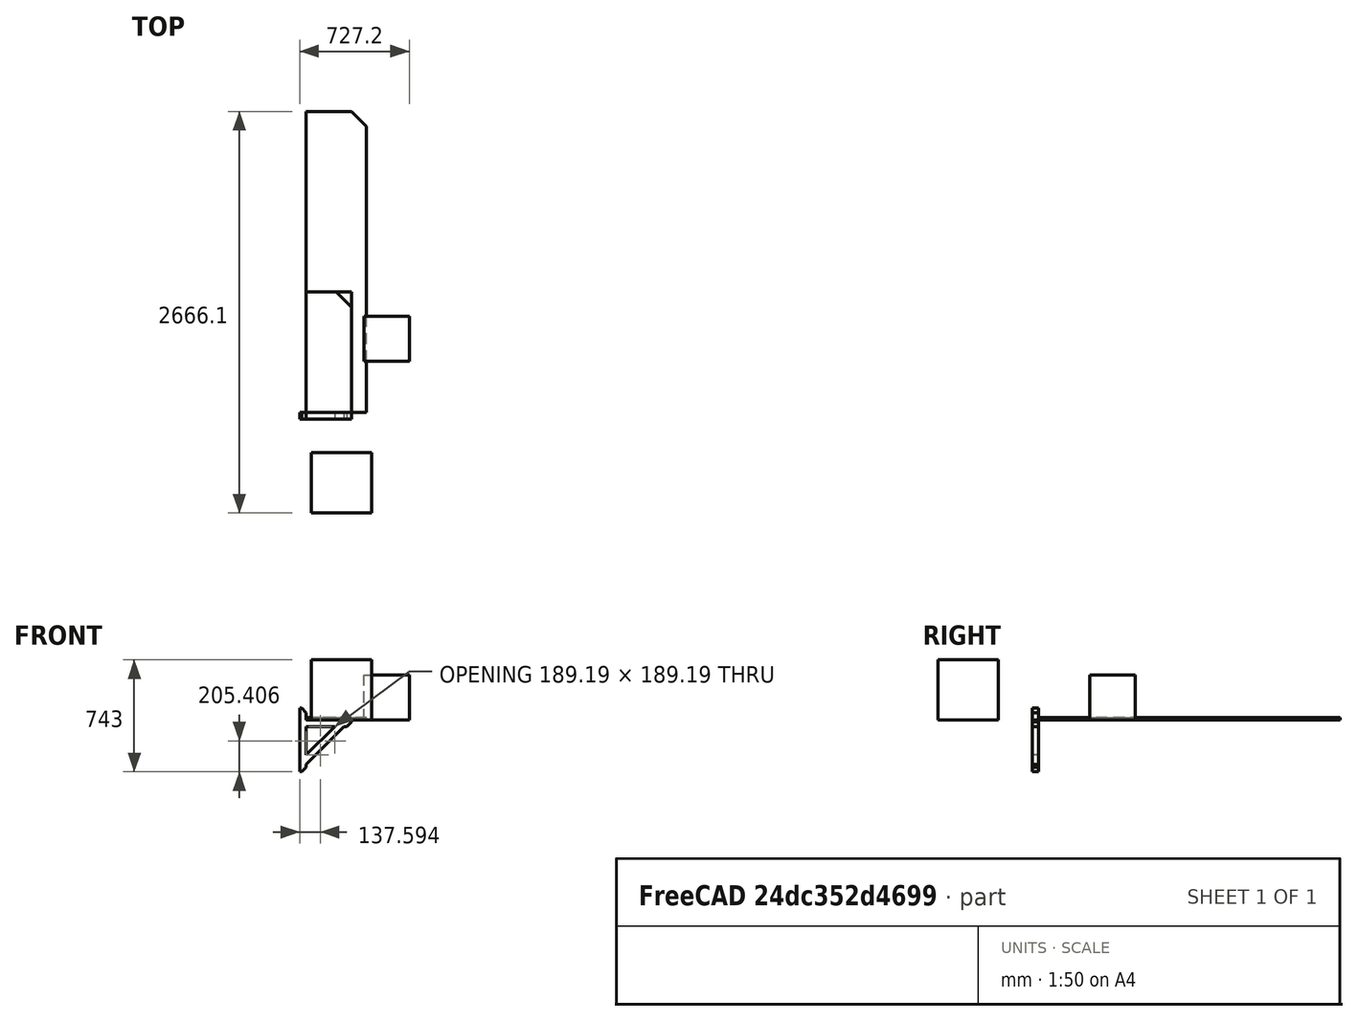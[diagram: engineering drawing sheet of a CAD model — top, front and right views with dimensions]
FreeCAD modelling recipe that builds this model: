
FCSTD DOCUMENT  (FreeCAD 1.0R39109 (Git))
Label: shed_shelves
License: All rights reserved
LicenseURL: https://en.wikipedia.org/wiki/All_rights_reserved
objects: App::FeaturePython×9, App::Link×7, App::Part×5, Sketcher::SketchObject×4, PartDesign::Pad×4, PartDesign::Body×4, Part::Box×2, PartDesign::Chamfer×2, App::DocumentObjectGroup×1, Assembly::JointGroup×1, Assembly::AssemblyObject×1
note: 32 computed .brp shape members not serialized (recipe doc carries the construction recipe); baked Part::Feature solids carry a one-line shape summary decoded from their .brp

FEATURE [Sketcher::SketchObject] Sketch
  ArcFitTolerance = 1e-06
  AttachmentSupport = -> [XY_Plane]
  FullyConstrained = true
  MakeInternals = false
  MapMode = 5
  sketch-geometry (4):
    g0: LineSegment StartX=0 StartY=0 StartZ=0 EndX=400 EndY=0 EndZ=0
    g1: LineSegment StartX=400 StartY=0 StartZ=0 EndX=400 EndY=2000 EndZ=0
    g2: LineSegment StartX=400 StartY=2000 StartZ=0 EndX=0 EndY=2000 EndZ=0
    g3: LineSegment StartX=0 StartY=2000 StartZ=0 EndX=0 EndY=0 EndZ=0
  constraints (11):
    c: Coincident(g0,g1)
    c: Coincident(g1,g2)
    c: Coincident(g2,g3)
    c: Coincident(g3,g0)
    c: Horizontal(g0)
    c: Horizontal(g2)
    c: Vertical(g1)
    c: Vertical(g3)
    c: Distance(g1,g3) = 400
    c: Distance(g0,g2) = 2000
    c: Coincident(g0,g-1)
FEATURE [PartDesign::Pad] Pad
  Direction = (0,0,1)
  Length = 18
  Length2 = 10
  Profile = -> Sketch
  ReferenceAxis = -> Sketch [N_Axis]
  Refine = true
  Suppressed = false
  Type = 0
FEATURE [Sketcher::SketchObject] Sketch001
  ArcFitTolerance = 1e-06
  AttachmentSupport = -> [XY_Plane002]
  FullyConstrained = true
  MakeInternals = false
  MapMode = 5
  sketch-geometry (4):
    g0: LineSegment StartX=0 StartY=0 StartZ=0 EndX=300 EndY=0 EndZ=0
    g1: LineSegment StartX=300 StartY=0 StartZ=0 EndX=300 EndY=800 EndZ=0
    g2: LineSegment StartX=300 StartY=800 StartZ=0 EndX=0 EndY=800 EndZ=0
    g3: LineSegment StartX=0 StartY=800 StartZ=0 EndX=0 EndY=0 EndZ=0
  constraints (11):
    c: Coincident(g0,g1)
    c: Coincident(g1,g2)
    c: Coincident(g2,g3)
    c: Coincident(g3,g0)
    c: Horizontal(g0)
    c: Horizontal(g2)
    c: Vertical(g1)
    c: Vertical(g3)
    c: Distance(g1,g3) = 300
    c: Distance(g0,g2) = 800
    c: Coincident(g0,g-1)
FEATURE [PartDesign::Pad] Pad001
  Direction = (0,0,1)
  Length = 18
  Length2 = 10
  Profile = -> Sketch001
  ReferenceAxis = -> Sketch001 [N_Axis]
  Refine = true
  Suppressed = false
  Type = 0
FEATURE [PartDesign::Body] Body001
  AllowCompound = false
  Group = -> [Sketch001,Pad001]
  Origin = -> Origin002
  Tip = -> Pad001
FEATURE [App::Part] Part001  label="Part_800x400x18"
  Group = -> [Body001]
  Origin = -> Origin003
FEATURE [Sketcher::SketchObject] Sketch002
  ArcFitTolerance = 1e-06
  AttachmentSupport = -> [XY_Plane004]
  FullyConstrained = true
  MakeInternals = false
  MapMode = 5
  sketch-geometry (4):
    g0: LineSegment StartX=0 StartY=0 StartZ=0 EndX=300 EndY=0 EndZ=0
    g1: LineSegment StartX=300 StartY=0 StartZ=0 EndX=300 EndY=800 EndZ=0
    g2: LineSegment StartX=300 StartY=800 StartZ=0 EndX=0 EndY=800 EndZ=0
    g3: LineSegment StartX=0 StartY=800 StartZ=0 EndX=0 EndY=0 EndZ=0
  constraints (11):
    c: Coincident(g0,g1)
    c: Coincident(g1,g2)
    c: Coincident(g2,g3)
    c: Coincident(g3,g0)
    c: Horizontal(g0)
    c: Horizontal(g2)
    c: Vertical(g1)
    c: Vertical(g3)
    c: Distance(g1,g3) = 300
    c: Distance(g0,g2) = 800
    c: Coincident(g0,g-1)
FEATURE [PartDesign::Pad] Pad002
  Direction = (0,0,1)
  Length = 18
  Length2 = 10
  Profile = -> Sketch002
  ReferenceAxis = -> Sketch002 [N_Axis]
  Refine = true
  Suppressed = false
  Type = 0
FEATURE [App::Link] Part_800x30x18  label="Part_800x30x019"
  LinkPlacement = pos=(0,0,0) rot=(0,0,1;4.71239rad)
  LinkedObject = -> Part002
  Placement = pos=(0,0,0) rot=(0,0,1;4.71239rad)
FEATURE [App::FeaturePython] GroundedJoint  # Assembly grounded joint (typed FeaturePython)
  ObjectToGround = -> Part_800x30x18
  Placement = pos=(0,0,0) rot=(0,0,1;4.71239rad)
FEATURE [App::Link] Part_800x400x18  label="Part_800x400x019"
  LinkPlacement = pos=(-300,-800,0) rot=(0,0,1;0rad)
  LinkedObject = -> Part001
  Placement = pos=(-300,-800,0) rot=(0,0,1;0rad)
FEATURE [App::Link] Part_2000x400x18  label="Part_2000x400x019"
  LinkPlacement = pos=(-300,-2800,0) rot=(0,0,1;0rad)
  LinkedObject = -> Part
  Placement = pos=(-300,-2800,0) rot=(0,0,1;0rad)
FEATURE [Part::Box] Box  label="Cube"
  AttacherType = Attacher::AttachEngine3D
  Height = 300
  Length = 300
  Placement = pos=(384.2,340,0) rot=(0,0,1;0rad)
  Width = 300
FEATURE [Part::Box] Box001  label="Cube001"
  AttacherType = Attacher::AttachEngine3D
  Height = 400
  Length = 400
  Placement = pos=(35,-666.1,0) rot=(0,0,1;0rad)
  Width = 400
FEATURE [App::Part] Part003
  Group = -> [Box,Box001]
  Origin = -> Origin007
  Placement = pos=(-336.4,-642.4,18) rot=(0,0,1;0rad)
FEATURE [PartDesign::Chamfer] Chamfer
  Angle = 45
  Base = -> Pad [Edge5]
  BaseFeature = -> Pad
  ChamferType = 0
  FlipDirection = false
  Refine = true
  Size = 100
  Size2 = 1
  SupportTransform = false
  Suppressed = false
  UseAllEdges = false
FEATURE [PartDesign::Body] Body
  AllowCompound = false
  Group = -> [Sketch,Pad,Chamfer]
  Origin = -> Origin
  Tip = -> Chamfer
FEATURE [App::Part] Part  label="Part_2000x400x18"
  Group = -> [Body]
  Origin = -> Origin001
FEATURE [PartDesign::Chamfer] Chamfer001
  Angle = 45
  Base = -> Pad002 [Edge5]
  BaseFeature = -> Pad002
  ChamferType = 0
  FlipDirection = false
  Refine = true
  Size = 100
  Size2 = 1
  SupportTransform = false
  Suppressed = false
  UseAllEdges = false
FEATURE [PartDesign::Body] Body002
  AllowCompound = false
  Group = -> [Sketch002,Pad002,Chamfer001]
  Origin = -> Origin004
  Tip = -> Chamfer001
FEATURE [App::Part] Part002  label="Part_800x30x18"
  Group = -> [Body002]
  Origin = -> Origin005
FEATURE [App::DocumentObjectGroup] Group  label="ShelvePlates"
  Group = -> [Part002,Part001,Part]
FEATURE [Sketcher::SketchObject] Sketch003
  ArcFitTolerance = 1e-06
  AttachmentSupport = -> [XZ_Plane009]
  FullyConstrained = true
  MakeInternals = false
  MapMode = 5
  Placement = pos=(0,0,0) rot=(1,0,0;1.5708rad)
  expr: Constraints[52] = .Constraints.edgeradii
  expr: Constraints[53] = .Constraints.edgeradii
  expr: Constraints[54] = .Constraints.wood_thinckness
  expr: Constraints[66] = .Constraints.wood_thinckness
  sketch-geometry (32):
    g0: LineSegment StartX=-43 StartY=80 StartZ=0 EndX=-43 EndY=-343 EndZ=0
    g1: LineSegment StartX=-43 StartY=-343 StartZ=0 EndX=-30 EndY=-343 EndZ=0
    g2: LineSegment StartX=0 StartY=-313 StartZ=0 EndX=0 EndY=50 EndZ=0
    g3: LineSegment StartX=-30 StartY=80 StartZ=0 EndX=-43 EndY=80 EndZ=0
    g4: LineSegment StartX=0 StartY=0 StartZ=0 EndX=0 EndY=-43 EndZ=0
    g5: LineSegment StartX=0 StartY=-43 StartZ=0 EndX=270 EndY=-43 EndZ=0
    g6: LineSegment StartX=300 StartY=-13 StartZ=0 EndX=300 EndY=0 EndZ=0
    g7: LineSegment StartX=300 StartY=0 StartZ=0 EndX=0 EndY=0 EndZ=0
    g8: LineSegment [constr] StartX=0 StartY=0 StartZ=0 EndX=400 EndY=0 EndZ=0
    g9: LineSegment [constr] StartX=400 StartY=0 StartZ=0 EndX=400 EndY=18 EndZ=0
    g10: LineSegment [constr] StartX=400 StartY=18 StartZ=0 EndX=0 EndY=18 EndZ=0
    g11: LineSegment [constr] StartX=0 StartY=18 StartZ=0 EndX=0 EndY=0 EndZ=0
    g12: LineSegment [constr] StartX=-43 StartY=-343 StartZ=0 EndX=300 EndY=0 EndZ=0
    g13: ArcOfCircle [constr] CenterX=-30 CenterY=50 CenterZ=0 NormalX=0 NormalY=0 NormalZ=1 AngleXU=0 Radius=30 StartAngle=0 EndAngle=1.5708
    g14: GeomPoint [constr] X=0 Y=80 Z=0
    g15: LineSegment StartX=0 StartY=50 StartZ=0 EndX=-30 EndY=80 EndZ=0
    g16: ArcOfCircle [constr] CenterX=270 CenterY=-13 CenterZ=0 NormalX=0 NormalY=0 NormalZ=1 AngleXU=0 Radius=30 StartAngle=4.71239 EndAngle=6.28319
    g17: GeomPoint [constr] X=300 Y=-43 Z=0
    g18: LineSegment StartX=270 StartY=-43 StartZ=0 EndX=300 EndY=-13 EndZ=0
    g19: ArcOfCircle [constr] CenterX=-30 CenterY=-313 CenterZ=0 NormalX=0 NormalY=0 NormalZ=1 AngleXU=0 Radius=30 StartAngle=4.71239 EndAngle=6.28319
    g20: GeomPoint [constr] X=0 Y=-343 Z=0
    g21: LineSegment StartX=-30 StartY=-343 StartZ=0 EndX=0 EndY=-313 EndZ=0
    g22: LineSegment StartX=3.6e-15 StartY=-293 StartZ=0 EndX=250 EndY=-43 EndZ=0
    g23: LineSegment [constr] StartX=-30.4056 StartY=-262.594 StartZ=0 EndX=219.594 EndY=-12.5944 EndZ=0
    g24: LineSegment [constr] StartX=-30.4056 StartY=-262.594 StartZ=0 EndX=3.6e-15 EndY=-293 EndZ=0
    g25: LineSegment [constr] StartX=219.594 StartY=-12.5944 StartZ=0 EndX=250 EndY=-43 EndZ=0
    g26: LineSegment StartX=3.6e-15 StartY=-293 StartZ=0 EndX=3.6e-15 EndY=-232.189 EndZ=0
    g27: LineSegment StartX=3.6e-15 StartY=-232.189 StartZ=0 EndX=189.189 EndY=-43 EndZ=0
    g28: LineSegment StartX=189.189 StartY=-43 StartZ=0 EndX=250 EndY=-43 EndZ=0
    g29: LineSegment [constr] StartX=-30 StartY=-343 StartZ=0 EndX=-43 EndY=-356 EndZ=0
    g30: LineSegment [constr] StartX=-30 StartY=80 StartZ=0 EndX=-43 EndY=93 EndZ=0
    g31: LineSegment [constr] StartX=-43 StartY=93 StartZ=0 EndX=-43 EndY=-356 EndZ=0
  constraints (88):
    c: Coincident(g3,g0)
    c: Vertical(g0)
    c: Vertical(g2)
    c: Horizontal(g1)
    c: Horizontal(g3)
    c: Coincident(g4,g5)
    c: Coincident(g6,g7)
    c: Coincident(g7,g4)
    c: Vertical(g4)
    c: Vertical(g6)
    c: Horizontal(g5)
    c: Horizontal(g7)
    c: PointOnObject(g4,g2)
    c: Distance(g17,g6) = 43  'wood_thinckness'
    c: Distance(g14,g4) = 80
    c: Coincident(g8,g9)
    c: Coincident(g9,g10)
    c: Coincident(g10,g11)
    c: Coincident(g11,g8)
    c: Horizontal(g8)
    c: Horizontal(g10)
    c: Vertical(g9)
    c: Vertical(g11)
    c: Coincident(g8,g-1)
    c: DistanceX(g10,g10) = 400
    c: Distance(g9,g9) = 18
    c: Coincident(g1,g0)
    c: Coincident(g4,g8)
    c: Coincident(g12,g0)
    c: Coincident(g12,g6)
    c: Angle(g10,g12) = 0.785398
    c: DistanceY(g0,g0) = 423
    c: Distance(g8,g6) = 100
    c: PointOnObject(g14,g2)
    c: PointOnObject(g14,g3)
    c: Tangent(g2,g13) = -1.5708
    c: Tangent(g3,g13) = -1.5708
    c: Coincident(g15,g2)
    c: Coincident(g15,g3)
    c: PointOnObject(g17,g5)
    c: PointOnObject(g17,g6)
    c: Tangent(g5,g16) = -1.5708
    c: Tangent(g6,g16) = -1.5708
    c: Coincident(g18,g5)
    c: Coincident(g18,g6)
    c: PointOnObject(g20,g1)
    c: PointOnObject(g20,g2)
    c: Tangent(g1,g19) = -1.5708
    c: Tangent(g2,g19) = -1.5708
    c: Coincident(g21,g1)
    c: Coincident(g21,g2)
    c: Radius(g16) = 30  'edgeradii'
    c: Radius(g19) = 30
    c: Radius(g13) = 30
    c: Distance(g0,g2) = 43
    c: DistanceX(g7,g7) = 300
    c: PointOnObject(g22,g2)
    c: PointOnObject(g22,g5)
    c: Parallel(g23,g22)
    c: Coincident(g24,g23)
    c: Coincident(g24,g22)
    c: Coincident(g25,g22)
    c: Coincident(g23,g25)
    c: Parallel(g24,g25)
    c: Perpendicular(g25,g23,g23) = 1.5708
    c: Parallel(g22,g12)
    c: Distance(g25,g25) = 43
    c: Coincident(g22,g26)
    c: PointOnObject(g26,g23)
    c: Vertical(g26)
    c: Coincident(g26,g27)
    c: Coincident(g28,g22)
    c: Coincident(g28,g27)
    c: PointOnObject(g27,g23)
    c: PointOnObject(g27,g5)
    c: Distance(g22,g22) = 353.553
    c: Distance(g2,g4) = 50
    c: Distance(g2,g22) = 20
    c: Coincident(g29,g1)
    c: Coincident(g30,g3)
    c: Parallel(g15,g30)
    c: Parallel(g29,g21)
    c: Coincident(g31,g30)
    c: Coincident(g31,g29)
    c: Vertical(g31)
    c: Vertical(g29,g0)
    c: DistanceY(g29,g30) = 449
    c: DistanceY(g29,g22) = 63
FEATURE [PartDesign::Pad] Pad003
  Direction = (0,-1,2e-16)
  Length = 43
  Length2 = 10
  Placement = pos=(0,0,0) rot=(1,0,0;1.5708rad)
  Profile = -> Sketch003
  ReferenceAxis = -> Sketch003 [N_Axis]
  Refine = true
  Suppressed = false
  Type = 0
FEATURE [PartDesign::Body] Body003
  AllowCompound = false
  Group = -> [Sketch003,Pad003]
  Origin = -> Origin009
  Tip = -> Pad003
FEATURE [App::Part] Part004  label="shelf_boy"
  Group = -> [Body003]
  Origin = -> Origin008
FEATURE [App::Link] shelf_boy  label="shelf_boy001"
  LinkPlacement = pos=(-300,-2688.5,-4.8e-15) rot=(0,0,1;0rad)
  LinkedObject = -> Part004
  Placement = pos=(-300,-2688.5,-4.8e-15) rot=(0,0,1;0rad)
FEATURE [App::Link] shelf_boy001  label="shelf_boy002"
  LinkPlacement = pos=(-300,-778.5,-4.8e-15) rot=(0,0,1;0rad)
  LinkedObject = -> Part004
  Placement = pos=(-300,-778.5,-4.8e-15) rot=(0,0,1;0rad)
FEATURE [App::Link] shelf_boy002  label="shelf_boy003"
  LinkPlacement = pos=(21.5,-1.11e-14,-7) rot=(0,0,1;4.71239rad)
  LinkedObject = -> Part004
  Placement = pos=(21.5,-1.11e-14,-7) rot=(0,0,1;4.71239rad)
FEATURE [App::Link] shelf_boy003  label="shelf_boy004"
  LinkPlacement = pos=(621.5,-0.000104777,-4.8e-15) rot=(0,0,1;4.71239rad)
  LinkedObject = -> Part004
  Placement = pos=(621.5,-0.000104777,-4.8e-15) rot=(0,0,1;4.71239rad)
FEATURE [App::FeaturePython] Parallel002  # Assembly joint (typed FeaturePython)
  Activated = true
  AngleMax = 0
  AngleMin = 0
  Detach1 = false
  Detach2 = false
  Distance = 0
  Distance2 = 0
  EnableAngleMax = false
  EnableAngleMin = false
  EnableLengthMax = false
  EnableLengthMin = false
  JointType = 6 (Parallel)
  LengthMax = 0
  LengthMin = 0
  Placement1 = pos=(0,-43,9.5e-15) rot=(0,1,0;3.14159rad)
  Placement2 = pos=(0,800,0) rot=(0,0,1;0rad)
  Reference1 = -> Assembly [shelf_boy002.Body003.Face8,shelf_boy002.Body003.Vertex10]
  Reference2 = -> Assembly [Part_800x400x18.Body001.Face5,Part_800x400x18.Body001.Vertex7]
FEATURE [App::FeaturePython] GroundedJoint001  # Assembly grounded joint (typed FeaturePython)
  ObjectToGround = -> Part_800x400x18
  Placement = pos=(-300,-800,0) rot=(0,0,1;0rad)
FEATURE [App::FeaturePython] GroundedJoint002  # Assembly grounded joint (typed FeaturePython)
  ObjectToGround = -> Part_2000x400x18
  Placement = pos=(-300,-2800,0) rot=(0,0,1;0rad)
FEATURE [App::FeaturePython] Fixed  # Assembly joint (typed FeaturePython)
  Activated = true
  AngleMax = 0
  AngleMin = 0
  Detach1 = false
  Detach2 = false
  Distance = 0
  Distance2 = 0
  EnableAngleMax = false
  EnableAngleMin = false
  EnableLengthMax = false
  EnableLengthMin = false
  JointType = 0 (Fixed)
  LengthMax = 0
  LengthMin = 0
  Placement1 = pos=(0,-21.5,25) rot=(-0.57735,0.57735,-0.57735;2.0944rad)
  Placement2 = pos=(300,800,18) rot=(0,-0.707107,0.707107;3.14159rad)
  Reference1 = -> Assembly [shelf_boy002.Body003.Face4,shelf_boy002.Body003.Face4]
  Reference2 = -> Assembly [Part_800x400x18.Body001.Face3,Part_800x400x18.Body001.Vertex6]
FEATURE [App::FeaturePython] Fixed001  # Assembly joint (typed FeaturePython)
  Activated = true
  AngleMax = 0
  AngleMin = 0
  Detach1 = false
  Detach2 = false
  Distance = 0
  Distance2 = 0
  EnableAngleMax = false
  EnableAngleMin = false
  EnableLengthMax = false
  EnableLengthMin = false
  JointType = 0 (Fixed)
  LengthMax = 0
  LengthMin = 0
  Placement1 = pos=(0,2000,0) rot=(-0.57735,-0.57735,0.57735;4.18879rad)
  Placement2 = pos=(0,-21.5,4.8e-15) rot=(-0.57735,-0.57735,0.57735;4.18879rad)
  Reference1 = -> Assembly [Part_2000x400x18.Body.Edge8,Part_2000x400x18.Body.Vertex7]
  Reference2 = -> Assembly [shelf_boy001.Body003.Edge12,shelf_boy001.Body003.Edge12]
FEATURE [App::FeaturePython] Fixed002  # Assembly joint (typed FeaturePython)
  Activated = true
  AngleMax = 0
  AngleMin = 0
  Detach1 = false
  Detach2 = false
  Distance = 0
  Distance2 = 0
  EnableAngleMax = false
  EnableAngleMin = false
  EnableLengthMax = false
  EnableLengthMin = false
  JointType = 0 (Fixed)
  LengthMax = 0
  LengthMin = 0
  Offset2 = pos=(0,0,-90) rot=(0,0,1;0rad)
  Placement1 = pos=(0,-21.5,4.8e-15) rot=(-0.57735,-0.57735,0.57735;4.18879rad)
  Placement2 = pos=(0,90,0) rot=(-0.57735,-0.57735,0.57735;4.18879rad)
  Reference1 = -> Assembly [shelf_boy.Body003.Edge12,shelf_boy.Body003.Edge12]
  Reference2 = -> Assembly [Part_2000x400x18.Body.Edge8,Part_2000x400x18.Body.Vertex6]
FEATURE [App::FeaturePython] Parallel  # Assembly joint (typed FeaturePython)
  Activated = true
  AngleMax = 0
  AngleMin = 0
  Detach1 = false
  Detach2 = false
  Distance = 0
  Distance2 = 0
  EnableAngleMax = false
  EnableAngleMin = false
  EnableLengthMax = false
  EnableLengthMin = false
  JointType = 6 (Parallel)
  LengthMax = 0
  LengthMin = 0
  Placement1 = pos=(0,800,0) rot=(0,0,1;0rad)
  Placement2 = pos=(0,0,0) rot=(0,1,0;3.14159rad)
  Reference1 = -> Assembly [Part_800x30x18.Body002.Face2,Part_800x30x18.Body002.Vertex7]
  Reference2 = -> Assembly [shelf_boy003.Body003.Face8,shelf_boy003.Body003.Vertex9]
FEATURE [App::FeaturePython] Fixed003  # Assembly joint (typed FeaturePython)
  Activated = true
  AngleMax = 0
  AngleMin = 0
  Detach1 = false
  Detach2 = false
  Distance = 0
  Distance2 = 0
  EnableAngleMax = false
  EnableAngleMin = false
  EnableLengthMax = false
  EnableLengthMin = false
  JointType = 0 (Fixed)
  LengthMax = 0
  LengthMin = 0
  Offset2 = pos=(0,0,200) rot=(0,0,1;0rad)
  Placement1 = pos=(0,-21.5,4.8e-15) rot=(-0.57735,-0.57735,0.57735;4.18879rad)
  Placement2 = pos=(0,600,0) rot=(-0.57735,-0.57735,0.57735;4.18879rad)
  Reference1 = -> Assembly [shelf_boy003.Body003.Edge12,shelf_boy003.Body003.Edge12]
  Reference2 = -> Assembly [Part_800x30x18.Body002.Edge8,Part_800x30x18.Body002.Vertex7]
FEATURE [Assembly::JointGroup] Joints
  Group = -> [GroundedJoint,Parallel002,GroundedJoint001,GroundedJoint002,Fixed,Fixed001,Fixed002,Parallel,Fixed003]
FEATURE [Assembly::AssemblyObject] Assembly
  Group = -> [Joints,Part_800x30x18,GroundedJoint,Part_800x400x18,Part_2000x400x18,Part003,shelf_boy,shelf_boy001,shelf_boy002,shelf_boy003,Parallel002,GroundedJoint001,GroundedJoint002,Fixed,Fixed001,Fixed002,Parallel,Fixed003]
  Origin = -> Origin006
  Type = Assembly
